# Revit family: IS_Kubo_T7141_BIM_FR
name_source: partatom
category: Plumbing Fixtures
revit_build: Autodesk Revit 2017 (Build: 20160225_1515(x64)
units: mm (PartAtom-declared; Revit-internal decimal feet)

## family parameters
Always vertical = No
Cut with Voids When Loaded = No
OmniClass Number = 23.45.05.14.21.11
OmniClass Title = Bath/Shower Units
Part Type = Normal
Room Calculation Point = No
Round Connector Dimension = Use Diameter
Shared = No
Work Plane-Based = No

## types (1)
- T7141EO - KUBO CAB DOUCHE 90X90 TSP ARG BRIL IC
    Accessoires = www.idealspec.fr
    Auteur = Ideal Standard
    BIMobject category = Shower screens
    BIMobject category code = sanitary-shower-screens
    BIMobject main category = Sanitary
    BIMobject main category code = sanitary
    BOSUseNativeGeometries = 1
    Bim-NomDuProjet = ISI_IdealStandard_ShowerEnclosures_KUBO_T7141EO
    Brand url = www.idealspec.fr
    Caractéristiques = KUBO QUAD 90X90 IC BRT/SIL CLR
    CodeBarre = 8014140370499
    Conformité = NF
    ConseilsDInstallation = 0
    Cost = 0 $
    Couleur = Argent, clair
    CoûtDeRemplacement = 0
    Date of publishing = 2018_07_24
    DateDeCréation = 2018_07_24
    Description = KUBO Cabine de douche verre transparent
 pour receveur 90 cm
    Dimensions = 1953 x 894 x 894mm
    EAN code = https://8014140370499
    Edition number = 1
    Espace = Interne
    Finition = Argent, clair
    Forme = Complexe
    Hauteur = 1953 mm
    IFC Classification = Sanitary Terminal
    IfcExportAs = SHOWER ENCLOSURES
    IfcExportType = IfcSanitaryTerminalType
    InformationsProduit = www.idealspec.fr
    Installation instructions = http://www.idealspec.fr
    Largeur = 894 mm
    Longueur = 894 mm
    Manufacturer name = Ideal Standard
    Marque = Ideal Standard
    Material main = Glass
    Matériel = Glass
    Model = T7141EO
    NBS Reference Code = 35-06-79
    NBS Reference Description = Shower Enclosures
    Nominal height = 0
    Nominal width = 895
    OmniClass Code = 23-31 17 00
    OmniClass Description = Showers
    Product Guid = 3085e6a1-c71a-4ebe-a7eb-f402633bd0c5
    Product SKU = T7141
    Product certification = http://www.idealspec.fr
    Product data url = https://bimobject.com
    Product family = Sanitary
    Product group = Shower enclosures
    Product name = KUBO QUAD 90X90 IC BRT/SIL CLR
    Product url = http://www.idealstandard.it
    Profondeur = 0 mm  [stored 0 ft]
    QR code = http://bimobject.com
    Raccordement = Plomberie
    Receveur = No
    Révision = 1
    Technical description = http://www.idealspec.fr
    TypeDeDouche = Enclosure
    URL = www.idealspec.fr
    Uniclass 1.4 Code = L72142
    Uniclass 1.4 Description = Shower screens, curtains
    Uniclass 2.0 Code = PR-35-06-79
    Uniclass 2.0 Description = Shower Enclosures
    Uniclass 2015 Code = Pr_40_20_06_79
    Uniclass 2015 Name = Shower enclosures
    Uniclass2015Code = Pr_40_20_06_79
    Uniclass2015Title = Shower enclosures
    Uniclass2015Version = Products v1.1
    UnitéDeMesure = Millimètres
    UnitéDeTemps = An
    UnitéMonétaire = €
    UrlDuFabricant = www.idealspec.fr
    Version = 1
    Weight Net (Kg) = 48
    Youtube clip = http://www.idealspec.fr

note: [stored X ft] marks values corroborated as IEEE doubles in the binary element streams (Revit-internal decimal feet)

## geometry (parser evidence)
native form markers: Sweep x1
no freeform markers — native parametric forms only
